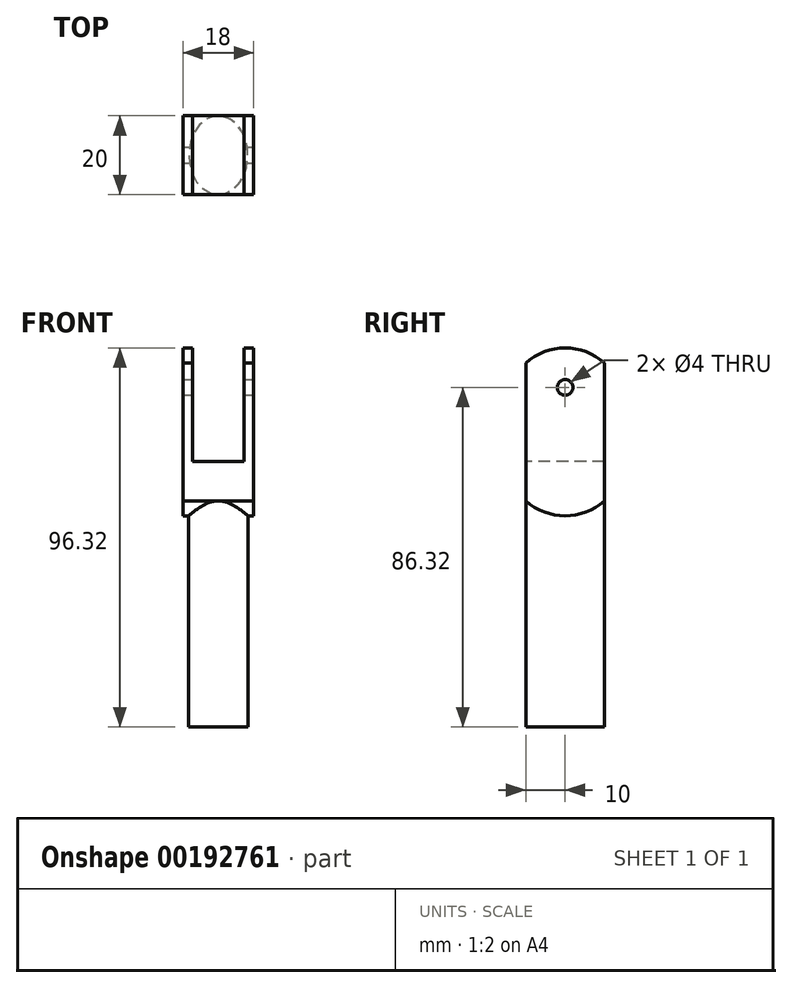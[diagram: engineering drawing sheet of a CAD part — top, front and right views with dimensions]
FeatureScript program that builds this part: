
annotation { "Feature Type Name" : "Feature", "Feature Type Description" : "" }
export const myFeature = defineFeature(function(context is Context, id is Id, definition is map)
    precondition{}
    {
        {
            var Q0;
            Q0=qCreatedBy(makeId("Top.planeOp"),FACE);
            var sketch = newSketch(context, id + "F0", { "sketchPlane" : qUnion([Q0])});
            skEllipse(sketch, "E0", {"center": v(0, 0) * mm, "majorRadius": 10 * mm, "minorRadius": 7.5 * mm, "majorAxis": v(0, -1)});
            skSolve(sketch);
        }
        {
            var Q0;
            Q0 = qSketchRegion(id + "F0", true);
            extrude(context, id + "F1", {"entities" : qUnion([Q0]), "depth" : 75 * mm});
        }
        {
            var Q0;
            Q0=qCreatedBy(makeId("Right.planeOp"),FACE);
            var sketch = newSketch(context, id + "F2", { "sketchPlane" : qUnion([Q0])});
            skLineSegment(sketch, "E1.bottom", {"start": v(10, 57.5) * mm, "end": v(-10, 57.5) * mm});
            skLineSegment(sketch, "E1.top", {"start": v(10, 92.5) * mm, "end": v(-10, 92.5) * mm});
            skLineSegment(sketch, "E1.left", {"start": v(10, 57.5) * mm, "end": v(10, 92.5) * mm});
            skLineSegment(sketch, "E1.right", {"start": v(-10, 57.5) * mm, "end": v(-10, 92.5) * mm});
            skPoint(sketch, "E1.middle", {"position": v(0, 75) * mm});
            skArc(sketch, "E2", {"start": v(10, 92.5) * mm, "mid": v(0, 96.32) * mm, "end": v(-10, 92.5) * mm});
            skArc(sketch, "E3", {"start": v(-10, 57.5) * mm, "mid": v(0, 53.68) * mm, "end": v(10, 57.5) * mm});
            skSolve(sketch);
        }
        {
            var Q0;
            Q0 = qSketchRegion(id + "F2", true);
            extrude(context, id + "F3", {"entities" : qUnion([Q0]), "operationType" : NewBodyOperationType.ADD, "depth" : 9 * mm, "hasSecondDirection" : true, "secondDirectionOppositeDirection" : true, "secondDirectionDepth" : 9 * mm});
        }
        {
            var Q0;
            Q0=qCreatedBy(makeId("Front.planeOp"),FACE);
            var sketch = newSketch(context, id + "F4", { "sketchPlane" : qUnion([Q0])});
            skLineSegment(sketch, "E4.bottom", {"start": v(6.5, 67.5) * mm, "end": v(-6.5, 67.5) * mm});
            skLineSegment(sketch, "E4.top", {"start": v(6.5, 132.5) * mm, "end": v(-6.5, 132.5) * mm});
            skLineSegment(sketch, "E4.left", {"start": v(6.5, 67.5) * mm, "end": v(6.5, 132.5) * mm});
            skLineSegment(sketch, "E4.right", {"start": v(-6.5, 67.5) * mm, "end": v(-6.5, 132.5) * mm});
            skPoint(sketch, "E4.middle", {"position": v(0, 100) * mm});
            skSolve(sketch);
        }
        {
            var Q0;
            Q0=makeQuery(id+"F4.imprint","IMPRINT",FACE,{"disambiguationData":[TD([[makeQuery(id+"F4.imprint","IMPRINT",EDGE,{"derivedFrom":sQuery(id+"F4.wireOp",EDGE,"E4.bottom")}),-1.0]])]});
            extrude(context, id + "F5", {"entities" : qUnion([Q0]), "operationType" : NewBodyOperationType.REMOVE, "oppositeDirection" : true, "depth" : 25 * mm, "hasSecondDirection" : true, "secondDirectionOppositeDirection" : false, "secondDirectionDepth" : 25 * mm});
        }
        {
            var Q0;
            Q0=makeQuery(id+"F3.opExtrude","CAP_FACE",FACE,{"disambiguationData":[OSD([sQuery(id+"F2.wireOp",EDGE,"E1.left"),sQuery(id+"F2.wireOp",EDGE,"E1.right"),sQuery(id+"F2.wireOp",EDGE,"E2"),sQuery(id+"F2.wireOp",EDGE,"E3")])],"isStart":false});
            var sketch = newSketch(context, id + "F6", { "sketchPlane" : qUnion([Q0])});
            skCircle(sketch, "E5", {"center": v(0, 86.32) * mm, "radius": 2 * mm});
            skSolve(sketch);
        }
        {
            var Q0;
            Q0 = qSketchRegion(id + "F6", true);
            extrude(context, id + "F7", {"entities" : qUnion([Q0]), "operationType" : NewBodyOperationType.REMOVE, "oppositeDirection" : true, "depth" : 25 * mm});
        }
    });
